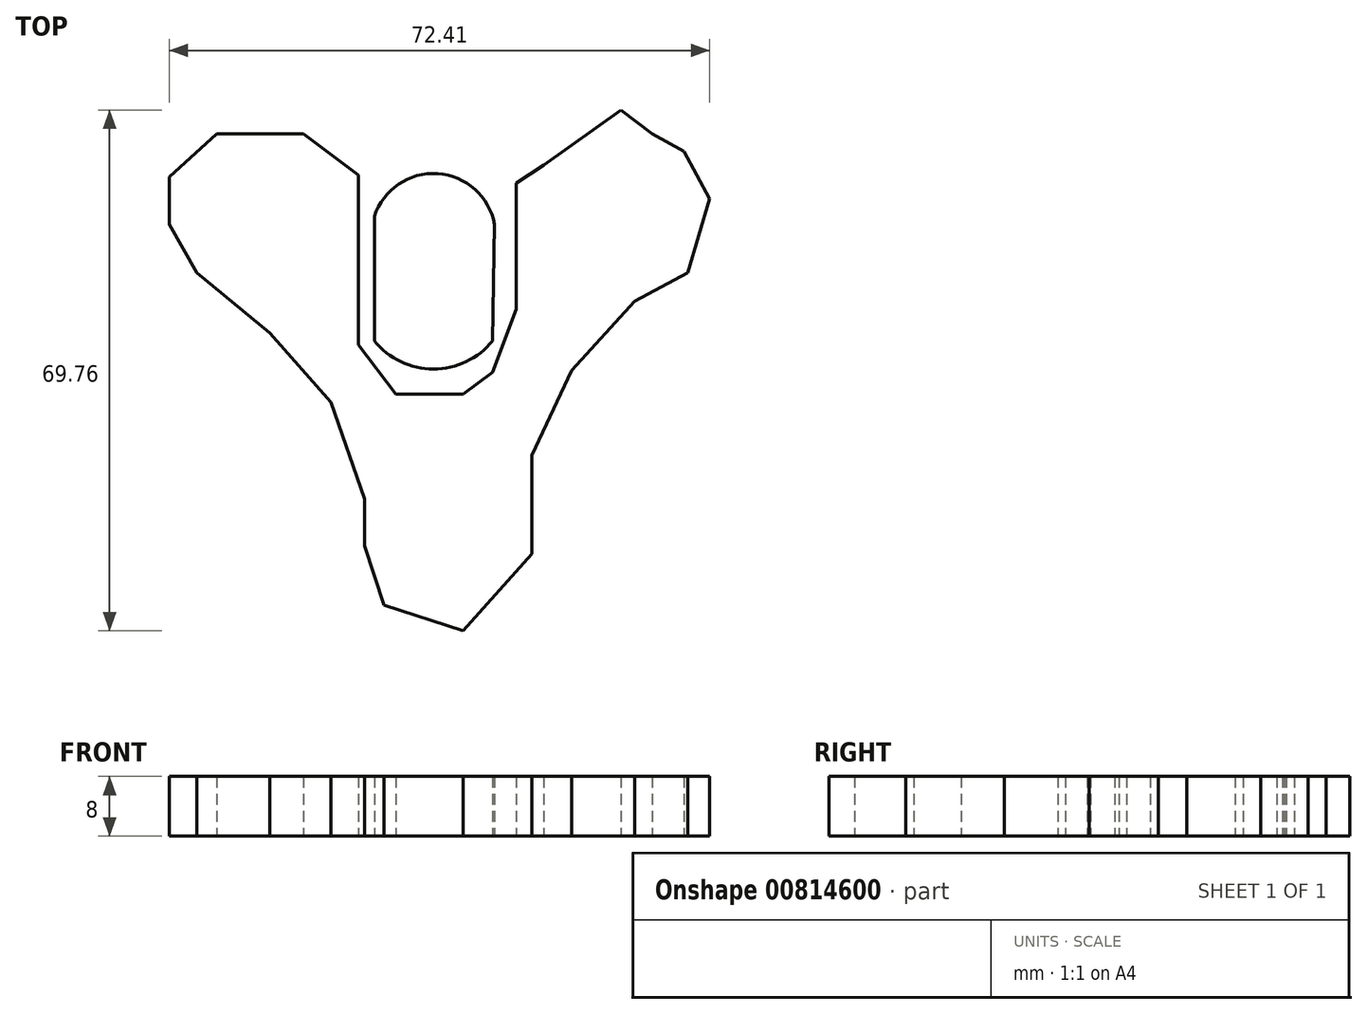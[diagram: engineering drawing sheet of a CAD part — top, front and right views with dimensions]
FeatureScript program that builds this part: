
annotation { "Feature Type Name" : "Feature", "Feature Type Description" : "" }
export const myFeature = defineFeature(function(context is Context, id is Id, definition is map)
    precondition{}
    {
        {
            var Q0;
            Q0=qCreatedBy(makeId("Top.planeOp"),FACE);
            var sketch = newSketch(context, id + "F0", { "sketchPlane" : qUnion([Q0])});
            skLineSegment(sketch, "E0", {"start": v(-10.7, 13.08) * mm, "end": v(-18.1, 18.63) * mm});
            skLineSegment(sketch, "E1", {"start": v(-18.1, 18.63) * mm, "end": v(-24.97, 18.63) * mm});
            skLineSegment(sketch, "E2", {"start": v(-24.97, 18.63) * mm, "end": v(-29.73, 18.63) * mm});
            skLineSegment(sketch, "E3", {"start": v(-29.73, 18.63) * mm, "end": v(-36.07, 12.82) * mm});
            skLineSegment(sketch, "E4", {"start": v(-36.07, 12.82) * mm, "end": v(-36.07, 6.47) * mm});
            skLineSegment(sketch, "E5", {"start": v(-36.07, 6.47) * mm, "end": v(-32.37, 0) * mm});
            skLineSegment(sketch, "E6", {"start": v(-32.37, 0) * mm, "end": v(-22.6, -8.06) * mm});
            skLineSegment(sketch, "E7", {"start": v(-22.6, -8.06) * mm, "end": v(-14.4, -17.3) * mm});
            skLineSegment(sketch, "E8", {"start": v(-14.4, -17.3) * mm, "end": v(-9.9, -30.26) * mm});
            skLineSegment(sketch, "E9", {"start": v(-9.9, -30.26) * mm, "end": v(-9.9, -36.6) * mm});
            skLineSegment(sketch, "E10", {"start": v(-9.9, -36.6) * mm, "end": v(-7.27, -44.53) * mm});
            skLineSegment(sketch, "E11", {"start": v(-7.27, -44.53) * mm, "end": v(3.3, -47.96) * mm});
            skLineSegment(sketch, "E12", {"start": v(3.3, -47.96) * mm, "end": v(12.55, -37.66) * mm});
            skLineSegment(sketch, "E13", {"start": v(12.55, -37.66) * mm, "end": v(12.55, -24.44) * mm});
            skLineSegment(sketch, "E14", {"start": v(12.55, -24.44) * mm, "end": v(17.84, -13.08) * mm});
            skLineSegment(sketch, "E15", {"start": v(17.84, -13.08) * mm, "end": v(26.3, -3.83) * mm});
            skLineSegment(sketch, "E16", {"start": v(26.3, -3.83) * mm, "end": v(33.43, 0) * mm});
            skLineSegment(sketch, "E17", {"start": v(33.43, 0) * mm, "end": v(36.34, 9.9) * mm});
            skLineSegment(sketch, "E18", {"start": v(36.34, 9.9) * mm, "end": v(32.9, 16.25) * mm});
            skLineSegment(sketch, "E19", {"start": v(32.9, 16.25) * mm, "end": v(28.67, 18.63) * mm});
            skLineSegment(sketch, "E20", {"start": v(28.67, 18.63) * mm, "end": v(24.44, 21.8) * mm});
            skLineSegment(sketch, "E21", {"start": v(24.44, 21.8) * mm, "end": v(14.14, 14.4) * mm});
            skLineSegment(sketch, "E22", {"start": v(14.14, 14.4) * mm, "end": v(10.44, 12.02) * mm});
            skLineSegment(sketch, "E23", {"start": v(10.44, 12.02) * mm, "end": v(10.44, -4.89) * mm});
            skLineSegment(sketch, "E24", {"start": v(10.44, -4.89) * mm, "end": v(7.27, -13.35) * mm});
            skLineSegment(sketch, "E25", {"start": v(7.27, -13.35) * mm, "end": v(3.3, -16.25) * mm});
            skLineSegment(sketch, "E26", {"start": v(3.3, -16.25) * mm, "end": v(-5.68, -16.25) * mm});
            skLineSegment(sketch, "E27", {"start": v(-5.68, -16.25) * mm, "end": v(-10.7, -9.65) * mm});
            skLineSegment(sketch, "E28", {"start": v(-10.7, -9.65) * mm, "end": v(-10.7, 13.08) * mm});
            skArc(sketch, "E29", {"start": v(7.53, 6.47) * mm, "mid": v(-0.12, 13.27) * mm, "end": v(-8.59, 7.53) * mm});
            skPoint(sketch, "E30.endSnap0", {"position": v(8.85, -9.12) * mm});
            skLineSegment(sketch, "E31", {"start": v(7.53, 6.47) * mm, "end": v(7.27, -9.12) * mm});
            skArc(sketch, "E32", {"start": v(-8.59, -9.12) * mm, "mid": v(-0.66, -12.9) * mm, "end": v(7.27, -9.12) * mm});
            skLineSegment(sketch, "E33", {"start": v(-8.59, 7.53) * mm, "end": v(-8.59, -9.12) * mm});
            skSolve(sketch);
        }
        {
            var Q0;
            Q0 = qSketchRegion(id + "F0", true);
            extrude(context, id + "F1", {"entities" : qUnion([Q0]), "depth" : 8 * mm, "offsetDistance" : 25 * mm});
        }
    });
